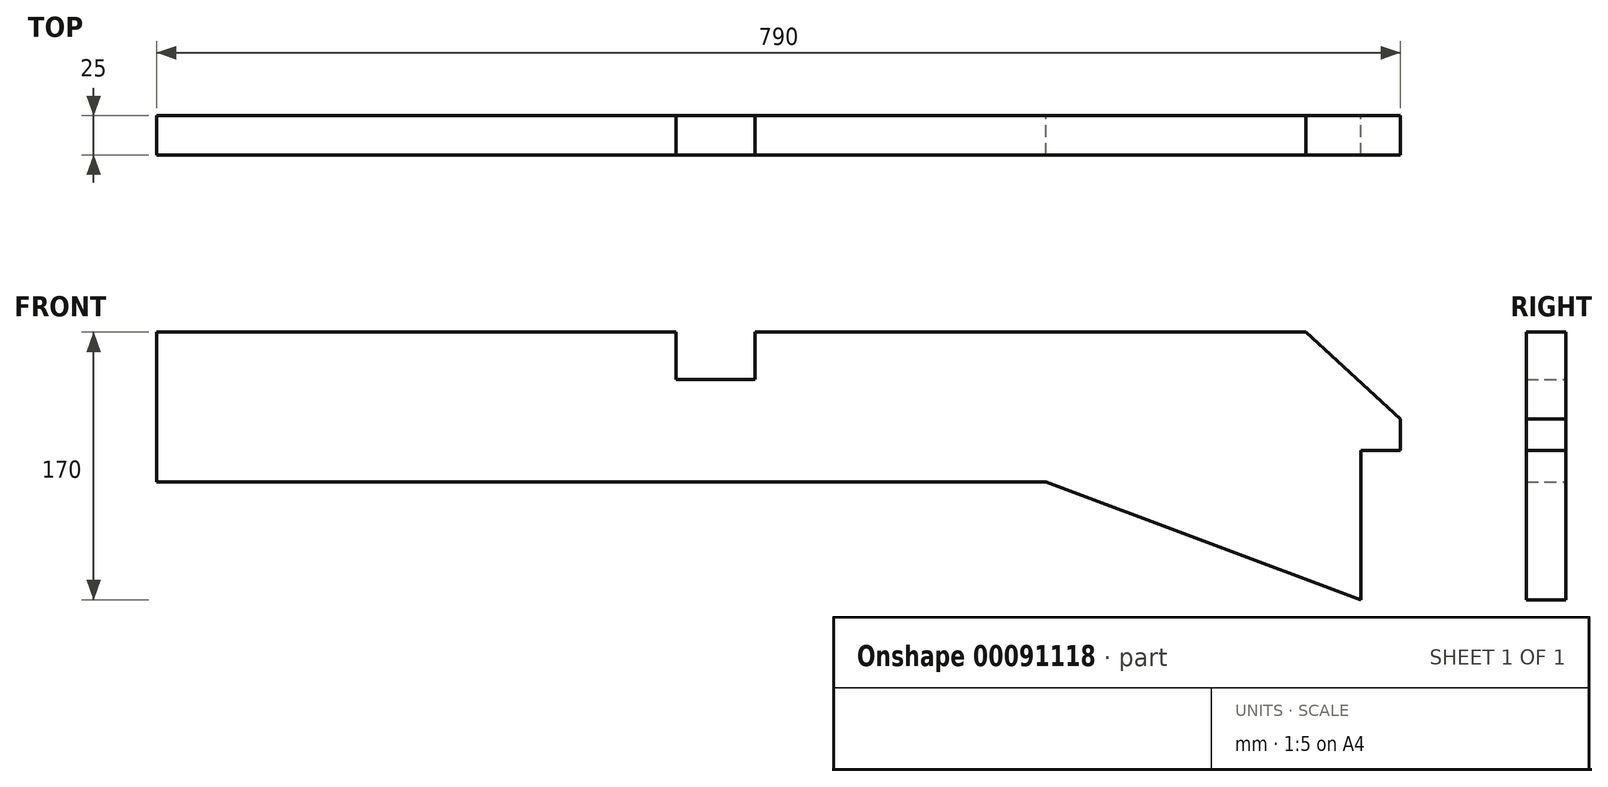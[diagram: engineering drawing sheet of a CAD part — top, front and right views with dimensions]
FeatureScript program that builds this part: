
annotation { "Feature Type Name" : "Feature", "Feature Type Description" : "" }
export const myFeature = defineFeature(function(context is Context, id is Id, definition is map)
    precondition{}
    {
        {
            var Q0;
            Q0=qCreatedBy(makeId("Front.planeOp"),FACE);
            var sketch = newSketch(context, id + "F0", { "sketchPlane" : qUnion([Q0])});
            skLineSegment(sketch, "E0", {"start": v(0, 0) * mm, "end": v(0, 95) * mm});
            skLineSegment(sketch, "E1", {"start": v(0, 95) * mm, "end": v(330, 95) * mm});
            skLineSegment(sketch, "E2", {"start": v(330, 95) * mm, "end": v(330, 65) * mm});
            skLineSegment(sketch, "E3", {"start": v(330, 65) * mm, "end": v(380, 65) * mm});
            skLineSegment(sketch, "E4", {"start": v(380, 65) * mm, "end": v(380, 95) * mm});
            skLineSegment(sketch, "E5", {"start": v(380, 95) * mm, "end": v(730, 95) * mm});
            skLineSegment(sketch, "E6", {"start": v(730, 95) * mm, "end": v(790, 40) * mm});
            skLineSegment(sketch, "E7", {"start": v(790, 40) * mm, "end": v(790, 20) * mm});
            skLineSegment(sketch, "E8", {"start": v(790, 20) * mm, "end": v(765, 20) * mm});
            skLineSegment(sketch, "E9", {"start": v(765, 20) * mm, "end": v(765, 0) * mm});
            skLineSegment(sketch, "E10", {"start": v(765, 0) * mm, "end": v(0, 0) * mm});
            skLineSegment(sketch, "E11", {"start": v(765, 0) * mm, "end": v(765, -75) * mm});
            skLineSegment(sketch, "E12", {"start": v(765, -75) * mm, "end": v(565, 0) * mm});
            skSolve(sketch);
        }
        {
            var Q0;
            {var subQ0=sQuery(id+"F0.wireOp",EDGE,"E0");Q0=makeQuery(id+"F0.imprint","IMPRINT",FACE,{"disambiguationData":[TD([[makeQuery(id+"F0.imprint","IMPRINT",EDGE,{"derivedFrom":subQ0}),-1.0]])]});}
            var Q1;
            {var subQ0=sQuery(id+"F0.wireOp",EDGE,"E11");Q1=makeQuery(id+"F0.imprint","IMPRINT",FACE,{"disambiguationData":[TD([[makeQuery(id+"F0.imprint","IMPRINT",EDGE,{"derivedFrom":subQ0}),-1.0]])]});}
            extrude(context, id + "F1", {"entities" : qUnion([Q0, Q1]), "depth" : 25 * mm});
        }
    });
